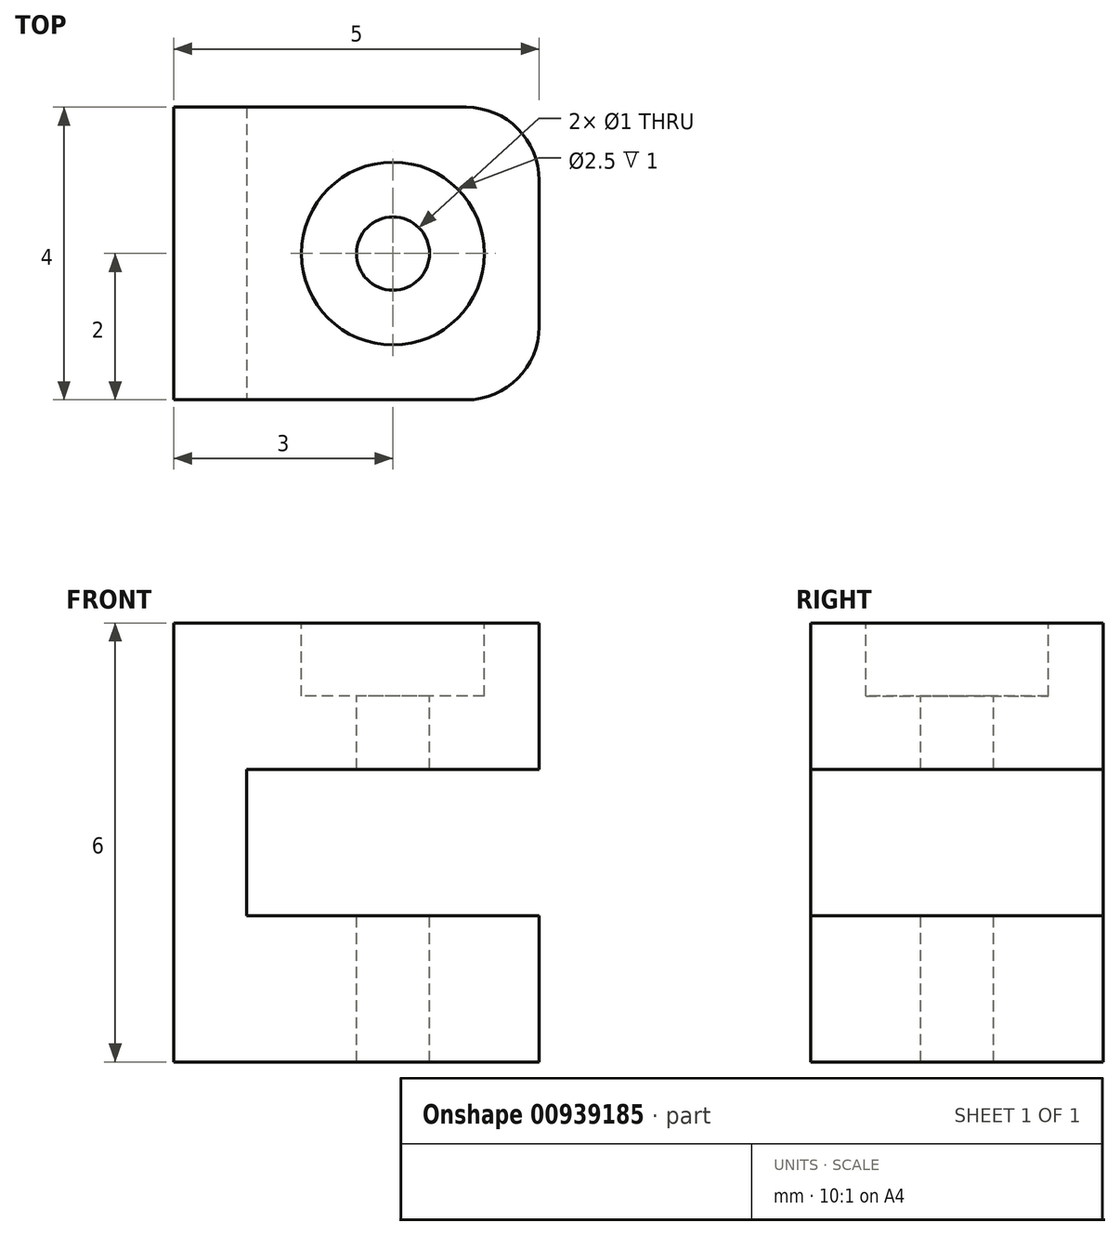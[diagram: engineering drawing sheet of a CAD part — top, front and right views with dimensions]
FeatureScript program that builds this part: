
annotation { "Feature Type Name" : "Feature", "Feature Type Description" : "" }
export const myFeature = defineFeature(function(context is Context, id is Id, definition is map)
    precondition{}
    {
        {
            var Q0;
            Q0=qCreatedBy(makeId("Top.planeOp"),FACE);
            var sketch = newSketch(context, id + "F0", { "sketchPlane" : qUnion([Q0])});
            skLineSegment(sketch, "E0.bottom", {"start": v(0, 0) * mm, "end": v(5, 0) * mm});
            skLineSegment(sketch, "E0.top", {"start": v(0, 4) * mm, "end": v(5, 4) * mm});
            skLineSegment(sketch, "E0.left", {"start": v(0, 0) * mm, "end": v(0, 4) * mm});
            skLineSegment(sketch, "E0.right", {"start": v(5, 0) * mm, "end": v(5, 4) * mm});
            skSolve(sketch);
        }
        {
            var Q0;
            Q0=makeQuery(id+"F0.imprint","IMPRINT",FACE,{"disambiguationData":[TD([[makeQuery(id+"F0.imprint","IMPRINT",EDGE,{"derivedFrom":sQuery(id+"F0.wireOp",EDGE,"E0.bottom")}),1.0]])]});
            extrude(context, id + "F1", {"entities" : qUnion([Q0]), "depth" : 6 * mm, "offsetDistance" : 25 * mm});
        }
        {
            var Q0;
            Q0=makeQuery(id+"F1.opExtrude","SWEPT_FACE",FACE,{"disambiguationData":[OSD([sQuery(id+"F0.wireOp",EDGE,"E0.bottom")])]});
            var sketch = newSketch(context, id + "F2", { "sketchPlane" : qUnion([Q0])});
            skLineSegment(sketch, "E1.bottom", {"start": v(5, 4) * mm, "end": v(1, 4) * mm});
            skLineSegment(sketch, "E1.top", {"start": v(5, 2) * mm, "end": v(1, 2) * mm});
            skLineSegment(sketch, "E1.left", {"start": v(5, 4) * mm, "end": v(5, 2) * mm});
            skLineSegment(sketch, "E1.right", {"start": v(1, 4) * mm, "end": v(1, 2) * mm});
            skSolve(sketch);
        }
        {
            var Q0;
            Q0=makeQuery(id+"F2.imprint","IMPRINT",FACE,{"disambiguationData":[TD([[makeQuery(id+"F2.imprint","IMPRINT",EDGE,{"derivedFrom":sQuery(id+"F2.wireOp",EDGE,"E1.bottom")}),1.0]])]});
            extrude(context, id + "F3", {"entities" : qUnion([Q0]), "operationType" : NewBodyOperationType.REMOVE, "oppositeDirection" : true, "depth" : 25 * mm, "offsetDistance" : 25 * mm});
        }
        {
            var Q0;
            Q0=makeQuery(id+"F1.opExtrude","CAP_FACE",FACE,{"disambiguationData":[OSD([sQuery(id+"F0.wireOp",EDGE,"E0.bottom"),sQuery(id+"F0.wireOp",EDGE,"E0.top"),sQuery(id+"F0.wireOp",EDGE,"E0.left"),sQuery(id+"F0.wireOp",EDGE,"E0.right")])],"isStart":false});
            var sketch = newSketch(context, id + "F4", { "sketchPlane" : qUnion([Q0])});
            skPoint(sketch, "E2", {"position": v(3, 2) * mm});
            skCircle(sketch, "E3", {"center": v(3, 2) * mm, "radius": 0.5 * mm});
            skSolve(sketch);
        }
        {
            var Q0;
            Q0=makeQuery(id+"F4.imprint","IMPRINT",FACE,{"disambiguationData":[TD([[makeQuery(id+"F4.imprint","IMPRINT",EDGE,{"derivedFrom":sQuery(id+"F4.wireOp",EDGE,"E3")}),1.0]])]});
            extrude(context, id + "F5", {"entities" : qUnion([Q0]), "operationType" : NewBodyOperationType.REMOVE, "oppositeDirection" : true, "depth" : 25 * mm, "offsetDistance" : 25 * mm});
        }
        {
            var Q0;
            Q0=makeQuery(id+"F1.opExtrude","CAP_FACE",FACE,{"disambiguationData":[OSD([sQuery(id+"F0.wireOp",EDGE,"E0.bottom"),sQuery(id+"F0.wireOp",EDGE,"E0.top"),sQuery(id+"F0.wireOp",EDGE,"E0.left"),sQuery(id+"F0.wireOp",EDGE,"E0.right")])],"isStart":false});
            var sketch = newSketch(context, id + "F6", { "sketchPlane" : qUnion([Q0])});
            skCircle(sketch, "E4", {"center": v(3, 2) * mm, "radius": 1.25 * mm});
            skSolve(sketch);
        }
        {
            var Q0;
            Q0=makeQuery(id+"F6.imprint","IMPRINT",FACE,{"disambiguationData":[TD([[makeQuery(id+"F6.imprint","IMPRINT",EDGE,{"derivedFrom":sQuery(id+"F6.wireOp",EDGE,"E4")}),1.0]])]});
            extrude(context, id + "F7", {"entities" : qUnion([Q0]), "operationType" : NewBodyOperationType.REMOVE, "oppositeDirection" : true, "depth" : 1 * mm, "offsetDistance" : 25 * mm});
        }
        {
            var Q0;
            {var subQ0=sQuery(id+"F0.wireOp",EDGE,"E0.bottom");var subQ1=sQuery(id+"F0.wireOp",EDGE,"E0.right");Q0=makeQuery(id+"F3.boolean.opBoolean","SPLIT",EDGE,{"disambiguationData":[TD([makeQuery(id+"F3.opExtrude","SWEPT_FACE",FACE,{"disambiguationData":[OSD([sQuery(id+"F2.wireOp",EDGE,"E1.bottom")])]})])],"derivedFrom":makeQuery(id+"F1.opExtrude","SWEPT_EDGE",EDGE,{"disambiguationData":[OSD([subQ0,subQ1])]})});}
            var Q1;
            {var subQ0=sQuery(id+"F0.wireOp",EDGE,"E0.right");var subQ1=sQuery(id+"F0.wireOp",EDGE,"E0.top");Q1=makeQuery(id+"F3.boolean.opBoolean","SPLIT",EDGE,{"disambiguationData":[TD([makeQuery(id+"F3.opExtrude","SWEPT_FACE",FACE,{"disambiguationData":[OSD([sQuery(id+"F2.wireOp",EDGE,"E1.bottom")])]})])],"derivedFrom":makeQuery(id+"F1.opExtrude","SWEPT_EDGE",EDGE,{"disambiguationData":[OSD([subQ1,subQ0])]})});}
            var Q2;
            {var subQ0=sQuery(id+"F0.wireOp",EDGE,"E0.right");var subQ1=sQuery(id+"F0.wireOp",EDGE,"E0.top");Q2=makeQuery(id+"F3.boolean.opBoolean","SPLIT",EDGE,{"disambiguationData":[TD([makeQuery(id+"F3.opExtrude","SWEPT_FACE",FACE,{"disambiguationData":[OSD([sQuery(id+"F2.wireOp",EDGE,"E1.top")])]})])],"derivedFrom":makeQuery(id+"F1.opExtrude","SWEPT_EDGE",EDGE,{"disambiguationData":[OSD([subQ1,subQ0])]})});}
            var Q3;
            {var subQ0=sQuery(id+"F0.wireOp",EDGE,"E0.bottom");var subQ1=sQuery(id+"F0.wireOp",EDGE,"E0.right");Q3=makeQuery(id+"F3.boolean.opBoolean","SPLIT",EDGE,{"disambiguationData":[TD([makeQuery(id+"F3.opExtrude","SWEPT_FACE",FACE,{"disambiguationData":[OSD([sQuery(id+"F2.wireOp",EDGE,"E1.top")])]})])],"derivedFrom":makeQuery(id+"F1.opExtrude","SWEPT_EDGE",EDGE,{"disambiguationData":[OSD([subQ0,subQ1])]})});}
            fillet(context, id + "F8", {"entities" : qUnion([Q0, Q1, Q2, Q3]), "radius" : 1 * mm, "tangentPropagation" : true, "allowEdgeOverflow" : false});
        }
    });
